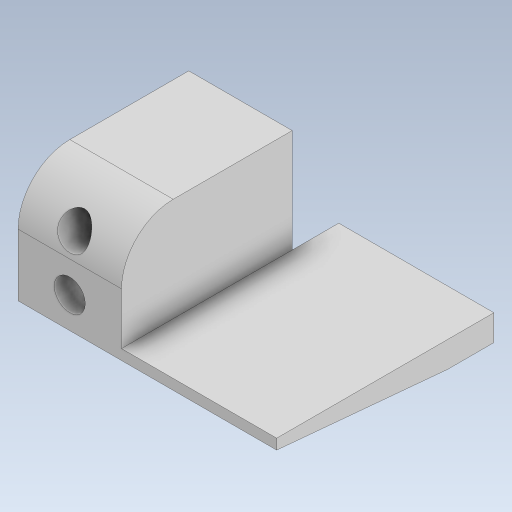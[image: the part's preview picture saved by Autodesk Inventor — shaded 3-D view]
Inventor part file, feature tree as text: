
AUTODESK INVENTOR PART (.ipt)
format: ipt  version: 2023.5 (Build 275446000, 446)  size: 226,304 bytes
history: native  units: in
note: dims shown in document units (in); Inventor stores cm internally (conversion verified against a paired STEP export)
features: extrude x12, sketch x10, plane x3, fillet x1
ambient origin geometry x8: Origin, YZ Plane, XZ Plane, XY Plane, X Axis, Y Axis, Z Axis, Center Point
bodies: Solid1 (feature_tree)
feature tree (26):
  sketch  "Sketch1"  dims[d0=0.7874in d1=0.5118in]
  extrude  "Extrusion1"  Depth=0.7874in
  extrude  "Extrusion2"  Depth=0.1181in
  extrude  "Extrusion3"  Depth=0.3937in TaperAngle=0.0deg
  plane  "Work Plane1"
  extrude  "Extrusion4"  Depth=0.7874in TaperAngle=0.0deg
  fillet  "Fillet1"  Radius=0.7874in
  extrude  "Extrusion5"  Depth=0.1181in
  plane  "Work Plane2"
  extrude  "Extrusion6"  Depth=0.1181in
  extrude  "Extrusion7"  Depth=0.7874in TaperAngle=0.0deg
  plane  "Work Plane3"
  extrude  "Extrusion8"  Depth=0.2362in
  extrude  "Extrusion9"  Depth=0.3937in TaperAngle=0.0deg
  extrude  "Extrusion10"  Depth=1.5748in TaperAngle=0.0deg
  extrude  "Extrusion11"  Depth=0.3937in TaperAngle=0.0deg
  extrude  "Extrusion12"  Depth=0.3543in
  sketch  "Sketch2"  dims[d2=0.7874in d3=0.1181in]
  sketch  "Sketch3"  dims[d4=0.3937in d5=0.0787in d6=0.0in]
  sketch  "Sketch4"  dims[d7=0.8661in d8=0.0in d9=0.0787in d10=0.0in d11=0.7874in d12=0.0in]
  sketch  "Sketch5"  dims[d13=0.3937in d14=0.1181in]
  sketch  "Sketch6"  dims[d15=0.2362in d16=0.1181in]
  sketch  "Sketch7"  dims[d18=0.2362in d19=0.7874in d20=0.0in]
  sketch  "Sketch8"  dims[d21=0.2362in d22=0.2362in]
  sketch  "Sketch9"  dims[d23=0.7874in d24=0.0in d25=0.3937in d26=0.0in]
  sketch  "Sketch10"  dims[d27=0.0787in d28=1.5748in d29=0.0in d30=0.3937in d31=0.0in d32=0.0394in d33=1.5748in d34=0.0in d35=0.3937in d36=0.0in d37=0.3543in d38=0.0in]
